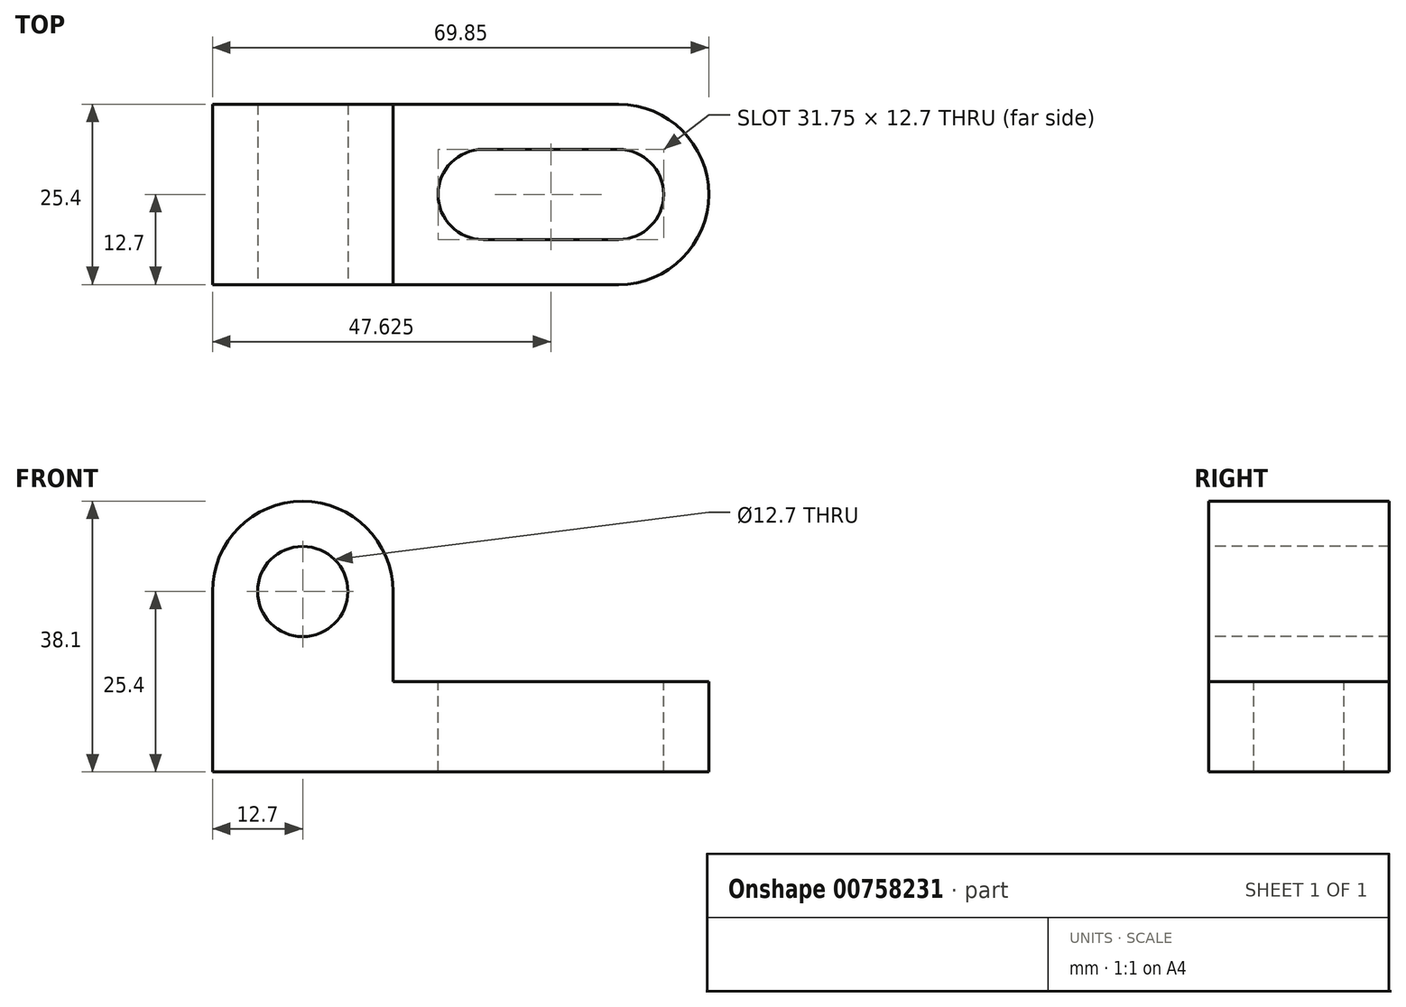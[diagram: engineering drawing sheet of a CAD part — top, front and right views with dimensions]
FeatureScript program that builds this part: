
annotation { "Feature Type Name" : "Feature", "Feature Type Description" : "" }
export const myFeature = defineFeature(function(context is Context, id is Id, definition is map)
    precondition{}
    {
        {
            var Q0;
            Q0=qCreatedBy(makeId("Front.planeOp"),FACE);
            var sketch = newSketch(context, id + "F0", { "sketchPlane" : qUnion([Q0])});
            skLineSegment(sketch, "E0", {"start": v(0, 0) * mm, "end": v(57.15, 0) * mm});
            skLineSegment(sketch, "E1", {"start": v(57.15, 0) * mm, "end": v(57.15, 12.7) * mm});
            skLineSegment(sketch, "E2", {"start": v(57.15, 12.7) * mm, "end": v(25.4, 12.7) * mm});
            skLineSegment(sketch, "E3", {"start": v(25.4, 12.7) * mm, "end": v(25.4, 25.4) * mm});
            skLineSegment(sketch, "E4", {"start": v(25.4, 25.4) * mm, "end": v(0, 25.4) * mm});
            skLineSegment(sketch, "E5", {"start": v(0, 25.4) * mm, "end": v(0, 0) * mm});
            skSolve(sketch);
        }
        {
            var Q0;
            Q0=makeQuery(id+"F0.imprint","IMPRINT",FACE,{"disambiguationData":[TD([[makeQuery(id+"F0.imprint","IMPRINT",EDGE,{"derivedFrom":sQuery(id+"F0.wireOp",EDGE,"E0")}),1.0]])]});
            extrude(context, id + "F1", {"entities" : qUnion([Q0]), "depth" : 25.4 * mm, "offsetDistance" : 25.4 * mm});
        }
        {
            var Q0;
            Q0=makeQuery(id+"F1.opExtrude","CAP_FACE",FACE,{"disambiguationData":[OSD([sQuery(id+"F0.wireOp",EDGE,"E0"),sQuery(id+"F0.wireOp",EDGE,"E1"),sQuery(id+"F0.wireOp",EDGE,"E2"),sQuery(id+"F0.wireOp",EDGE,"E3"),sQuery(id+"F0.wireOp",EDGE,"E4"),sQuery(id+"F0.wireOp",EDGE,"E5")])],"isStart":false});
            var sketch = newSketch(context, id + "F2", { "sketchPlane" : qUnion([Q0])});
            skArc(sketch, "E6", {"start": v(25.4, 25.4) * mm, "mid": v(12.7, 38.1) * mm, "end": v(0, 25.4) * mm});
            skCircle(sketch, "E7", {"center": v(12.7, 25.4) * mm, "radius": 6.35 * mm});
            skSolve(sketch);
        }
        {
            var Q0;
            Q0=makeQuery(id+"F1.opExtrude","SWEPT_FACE",FACE,{"disambiguationData":[OSD([sQuery(id+"F0.wireOp",EDGE,"E2")])]});
            var sketch = newSketch(context, id + "F3", { "sketchPlane" : qUnion([Q0])});
            skArc(sketch, "E8", {"start": v(57.15, -25.4) * mm, "mid": v(69.85, -12.7) * mm, "end": v(57.15, 0) * mm});
            skSolve(sketch);
        }
        {
            var Q0;
            Q0 = qSketchRegion(id + "F3", true);
            var Q1;
            Q1=makeQuery(id+"F3.imprint","IMPRINT",FACE,{"disambiguationData":[TD([[makeQuery(id+"F3.imprint","IMPRINT",EDGE,{"derivedFrom":sQuery(id+"F3.wireOp",EDGE,"E8")}),1.0]])]});
            extrude(context, id + "F4", {"entities" : qUnion([Q0, Q1]), "operationType" : NewBodyOperationType.ADD, "depth" : 0 * mm, "offsetDistance" : 25.4 * mm, "hasSecondDirection" : true, "secondDirectionOppositeDirection" : true, "secondDirectionDepth" : 12.7 * mm});
        }
        {
            var Q0;
            Q0=makeQuery(id+"F2.imprint","IMPRINT",FACE,{"disambiguationData":[TD([[makeQuery(id+"F2.imprint","IMPRINT",EDGE,{"derivedFrom":sQuery(id+"F2.wireOp",EDGE,"E6")}),1.0]])]});
            extrude(context, id + "F5", {"entities" : qUnion([Q0]), "operationType" : NewBodyOperationType.ADD, "depth" : 0 * mm, "offsetDistance" : 25.4 * mm, "hasSecondDirection" : true, "secondDirectionOppositeDirection" : true, "secondDirectionDepth" : 25.4 * mm});
        }
        {
            var Q0;
            {var subQ0=sQuery(id+"F0.wireOp",EDGE,"E2");Q0=makeQuery(id+"F4.boolean.opBoolean","MERGE",FACE,{"derivedFrom":[makeQuery(id+"F1.opExtrude","SWEPT_FACE",FACE,{"disambiguationData":[OSD([subQ0])]}),makeQuery(id+"F4.opExtrude","CAP_FACE",FACE,{"disambiguationData":[OSD([sQuery(id+"F0.wireOp",EDGE,"E1"),subQ0,sQuery(id+"F3.wireOp",EDGE,"E8")])],"isStart":false})]});}
            var sketch = newSketch(context, id + "F6", { "sketchPlane" : qUnion([Q0])});
            skLineSegment(sketch, "E9", {"start": v(38.1, -19.05) * mm, "end": v(38.1, -6.35) * mm});
            skLineSegment(sketch, "E10", {"start": v(38.1, -6.35) * mm, "end": v(57.15, -6.35) * mm});
            skLineSegment(sketch, "E11", {"start": v(38.1, -19.05) * mm, "end": v(57.15, -19.05) * mm});
            skLineSegment(sketch, "E12", {"start": v(57.15, -19.05) * mm, "end": v(57.15, -6.35) * mm});
            skArc(sketch, "E13", {"start": v(38.1, -6.35) * mm, "mid": v(31.75, -12.7) * mm, "end": v(38.1, -19.05) * mm});
            skArc(sketch, "E14", {"start": v(57.15, -19.05) * mm, "mid": v(63.5, -12.7) * mm, "end": v(57.15, -6.35) * mm});
            skSolve(sketch);
        }
        {
            var Q0;
            Q0=makeQuery(id+"F6.imprint","IMPRINT",FACE,{"disambiguationData":[TD([[makeQuery(id+"F6.imprint","IMPRINT",EDGE,{"derivedFrom":sQuery(id+"F6.wireOp",EDGE,"E9")}),1.0]])]});
            var Q1;
            Q1=makeQuery(id+"F6.imprint","IMPRINT",FACE,{"disambiguationData":[TD([[makeQuery(id+"F6.imprint","IMPRINT",EDGE,{"derivedFrom":sQuery(id+"F6.wireOp",EDGE,"E9")}),-1.0]])]});
            var Q2;
            Q2=makeQuery(id+"F6.imprint","IMPRINT",FACE,{"disambiguationData":[TD([[makeQuery(id+"F6.imprint","IMPRINT",EDGE,{"derivedFrom":sQuery(id+"F6.wireOp",EDGE,"E12")}),-1.0]])]});
            extrude(context, id + "F7", {"entities" : qUnion([Q0, Q1, Q2]), "operationType" : NewBodyOperationType.REMOVE, "oppositeDirection" : true, "depth" : 12.7 * mm, "offsetDistance" : 25.4 * mm, "hasSecondDirection" : true, "secondDirectionOppositeDirection" : false, "secondDirectionDepth" : 25.4 * mm});
        }
        {
            var Q0;
            {var subQ0=sQuery(id+"F2.wireOp",EDGE,"E7");var subQ1=makeQuery(id+"F1.opExtrude","CAP_EDGE",EDGE,{"disambiguationData":[OSD([sQuery(id+"F0.wireOp",EDGE,"E4")])],"isStart":false});var subQ2=makeQuery(id+"F2.imprint","INTERSECT",VERTEX,{"disambiguationData":[OD(0.0)],"derivedFrom":[subQ1,subQ0]});Q0=makeQuery(id+"F2.imprint","IMPRINT",FACE,{"disambiguationData":[TD([[makeQuery(id+"F2.imprint","IMPRINT",EDGE,{"disambiguationData":[TD([[subQ2,1.0]])],"derivedFrom":subQ0}),1.0]])]});}
            var Q1;
            {var subQ0=sQuery(id+"F2.wireOp",EDGE,"E7");var subQ1=makeQuery(id+"F1.opExtrude","CAP_EDGE",EDGE,{"disambiguationData":[OSD([sQuery(id+"F0.wireOp",EDGE,"E4")])],"isStart":false});var subQ2=makeQuery(id+"F2.imprint","INTERSECT",VERTEX,{"disambiguationData":[OD(0.0)],"derivedFrom":[subQ1,subQ0]});Q1=makeQuery(id+"F2.imprint","IMPRINT",FACE,{"disambiguationData":[TD([[makeQuery(id+"F2.imprint","IMPRINT",EDGE,{"disambiguationData":[TD([[subQ2,-1.0]])],"derivedFrom":subQ0}),1.0]])]});}
            extrude(context, id + "F8", {"entities" : qUnion([Q0, Q1]), "operationType" : NewBodyOperationType.REMOVE, "depth" : 25.4 * mm, "offsetDistance" : 25.4 * mm, "hasSecondDirection" : true, "secondDirectionOppositeDirection" : true, "secondDirectionDepth" : 25.4 * mm});
        }
    });
